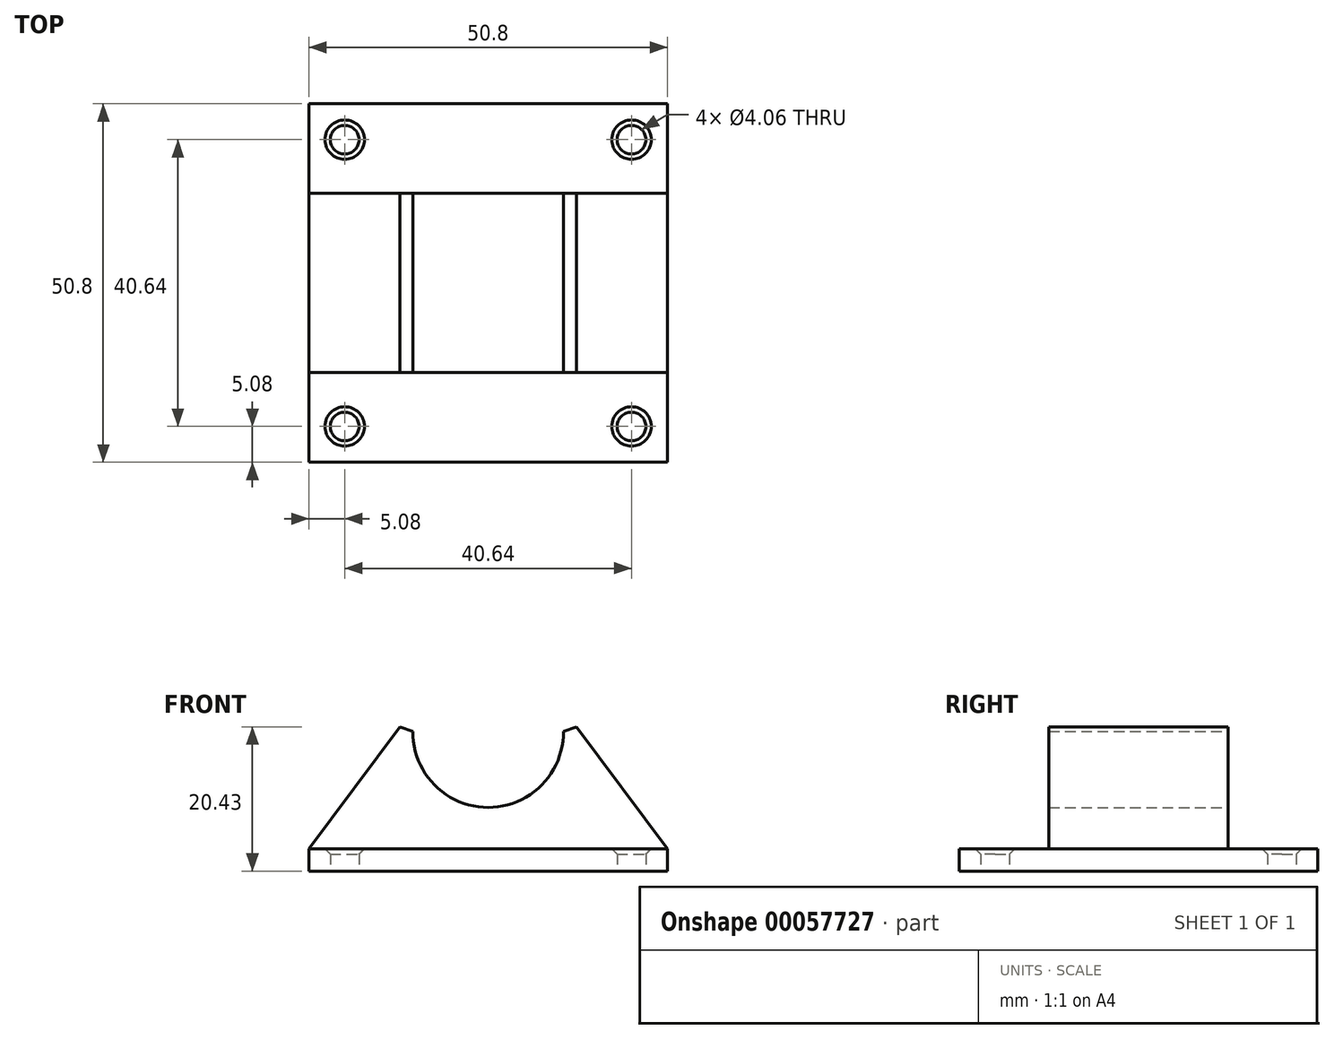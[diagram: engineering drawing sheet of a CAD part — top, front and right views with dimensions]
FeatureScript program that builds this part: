
annotation { "Feature Type Name" : "Feature", "Feature Type Description" : "" }
export const myFeature = defineFeature(function(context is Context, id is Id, definition is map)
    precondition{}
    {
        {
            var Q0;
            Q0=qCreatedBy(makeId("Top.planeOp"),FACE);
            var sketch = newSketch(context, id + "F0", { "sketchPlane" : qUnion([Q0])});
            skLineSegment(sketch, "E0.rect.bottom", {"start": v(-25.4, 25.4) * mm, "end": v(25.4, 25.4) * mm});
            skLineSegment(sketch, "E0.rect.top", {"start": v(-25.4, -25.4) * mm, "end": v(25.4, -25.4) * mm});
            skLineSegment(sketch, "E0.rect.left", {"start": v(-25.4, 25.4) * mm, "end": v(-25.4, -25.4) * mm});
            skLineSegment(sketch, "E0.rect.right", {"start": v(25.4, 25.4) * mm, "end": v(25.4, -25.4) * mm});
            skPoint(sketch, "E0.rect.middle", {"position": v(0, 0) * mm});
            skSolve(sketch);
        }
        {
            var Q0;
            Q0=makeQuery(id+"F0.imprint","IMPRINT",FACE,{"disambiguationData":[TD([[makeQuery(id+"F0.imprint","IMPRINT",EDGE,{"derivedFrom":sQuery(id+"F0.wireOp",EDGE,"E0.rect.bottom")}),-1.0]])]});
            extrude(context, id + "F1", {"entities" : qUnion([Q0]), "depth" : 3.17 * mm});
        }
        {
            var Q0;
            Q0=qCreatedBy(makeId("Front.planeOp"),FACE);
            var sketch = newSketch(context, id + "F2", { "sketchPlane" : qUnion([Q0])});
            skArc(sketch, "E1", {"start": v(-9.64, 24.26) * mm, "mid": v(0, 9.02) * mm, "end": v(9.64, 24.26) * mm});
            skLineSegment(sketch, "E2", {"start": v(9.64, 24.26) * mm, "end": v(-9.64, 24.26) * mm, "construction": true});
            skLineSegment(sketch, "E3.0", {"start": v(-25.4, 3.18) * mm, "end": v(25.4, 3.18) * mm});
            skLineSegment(sketch, "E4", {"start": v(-9.64, 24.26) * mm, "end": v(-25.4, 3.17) * mm});
            skLineSegment(sketch, "E5", {"start": v(9.64, 24.26) * mm, "end": v(25.4, 3.18) * mm});
            skSolve(sketch);
        }
        {
            var Q0;
            Q0=makeQuery(id+"F2.imprint","IMPRINT",FACE,{"disambiguationData":[TD([[makeQuery(id+"F2.imprint","IMPRINT",EDGE,{"derivedFrom":sQuery(id+"F2.wireOp",EDGE,"E1")}),-1.0]])]});
            extrude(context, id + "F3", {"entities" : qUnion([Q0]), "operationType" : NewBodyOperationType.ADD, "endBound" : BoundingType.SYMMETRIC, "depth" : 25.4 * mm});
        }
        {
            var Q0;
            Q0=makeQuery(id+"F3.opExtrude","SWEPT_EDGE",EDGE,{"disambiguationData":[OSD([sQuery(id+"F2.wireOp",EDGE,"E1"),sQuery(id+"F2.wireOp",EDGE,"E4")])]});
            var Q1;
            Q1=makeQuery(id+"F3.opExtrude","SWEPT_EDGE",EDGE,{"disambiguationData":[OSD([sQuery(id+"F2.wireOp",EDGE,"E1"),sQuery(id+"F2.wireOp",EDGE,"E5")])]});
            chamfer(context, id + "F4", {"entities" : qUnion([Q0, Q1]), "width" : 1.02 * mm, "tangentPropagation" : true});
        }
        {
            var Q0;
            Q0=makeQuery(id+"F1.opExtrude","CAP_FACE",FACE,{"disambiguationData":[OSD([sQuery(id+"F0.wireOp",EDGE,"E0.rect.bottom"),sQuery(id+"F0.wireOp",EDGE,"E0.rect.top"),sQuery(id+"F0.wireOp",EDGE,"E0.rect.left"),sQuery(id+"F0.wireOp",EDGE,"E0.rect.right")])],"isStart":true});
            var sketch = newSketch(context, id + "F5", { "sketchPlane" : qUnion([Q0])});
            skLineSegment(sketch, "E6.0", {"start": v(-20.32, 20.32) * mm, "end": v(20.32, 20.32) * mm, "construction": true});
            skLineSegment(sketch, "E6.1", {"start": v(-20.32, -20.32) * mm, "end": v(-20.32, 20.32) * mm, "construction": true});
            skLineSegment(sketch, "E6.2", {"start": v(-20.32, -20.32) * mm, "end": v(20.32, -20.32) * mm, "construction": true});
            skLineSegment(sketch, "E6.3", {"start": v(20.32, -20.32) * mm, "end": v(20.32, 20.32) * mm, "construction": true});
            skCircle(sketch, "E7", {"center": v(-20.32, 20.32) * mm, "radius": 2.03 * mm});
            skCircle(sketch, "E8", {"center": v(20.32, 20.32) * mm, "radius": 2.03 * mm});
            skCircle(sketch, "E9", {"center": v(20.32, -20.32) * mm, "radius": 2.03 * mm});
            skCircle(sketch, "E10", {"center": v(-20.32, -20.32) * mm, "radius": 2.03 * mm});
            skSolve(sketch);
        }
        {
            var Q0;
            Q0=makeQuery(id+"F5.imprint","IMPRINT",FACE,{"disambiguationData":[TD([[makeQuery(id+"F5.imprint","IMPRINT",EDGE,{"derivedFrom":sQuery(id+"F5.wireOp",EDGE,"E7")}),1.0]])]});
            var Q1;
            Q1=makeQuery(id+"F5.imprint","IMPRINT",FACE,{"disambiguationData":[TD([[makeQuery(id+"F5.imprint","IMPRINT",EDGE,{"derivedFrom":sQuery(id+"F5.wireOp",EDGE,"E10")}),1.0]])]});
            var Q2;
            Q2=makeQuery(id+"F5.imprint","IMPRINT",FACE,{"disambiguationData":[TD([[makeQuery(id+"F5.imprint","IMPRINT",EDGE,{"derivedFrom":sQuery(id+"F5.wireOp",EDGE,"E8")}),1.0]])]});
            var Q3;
            Q3=makeQuery(id+"F5.imprint","IMPRINT",FACE,{"disambiguationData":[TD([[makeQuery(id+"F5.imprint","IMPRINT",EDGE,{"derivedFrom":sQuery(id+"F5.wireOp",EDGE,"E9")}),1.0]])]});
            var Q4;
            Q4=sQuery(id+"F5.wireOp",EDGE,"E7");
            var Q5;
            Q5=sQuery(id+"F5.wireOp",EDGE,"E10");
            var Q6;
            Q6=sQuery(id+"F5.wireOp",EDGE,"E9");
            var Q7;
            Q7=sQuery(id+"F5.wireOp",EDGE,"E8");
            extrude(context, id + "F6", {"entities" : qUnion([Q0, Q1, Q2, Q3]), "operationType" : NewBodyOperationType.REMOVE, "surfaceEntities" : qUnion([Q4, Q5, Q6, Q7]), "oppositeDirection" : true, "depth" : 25.4 * mm});
        }
        {
            var Q0;
            {var subQ2=sQuery(id+"F0.wireOp",EDGE,"E0.rect.right");var subQ3=sQuery(id+"F0.wireOp",EDGE,"E0.rect.left");var subQ4=sQuery(id+"F0.wireOp",EDGE,"E0.rect.top");Q0=makeQuery(id+"F6.boolean.opBoolean","INTERSECT",EDGE,{"derivedFrom":[makeQuery(id+"F3.boolean.opBoolean","SPLIT",FACE,{"disambiguationData":[TD([makeQuery(id+"F1.opExtrude","SWEPT_FACE",FACE,{"disambiguationData":[OSD([subQ4])]})])],"derivedFrom":makeQuery(id+"F1.opExtrude","CAP_FACE",FACE,{"disambiguationData":[OSD([sQuery(id+"F0.wireOp",EDGE,"E0.rect.bottom"),subQ4,subQ3,subQ2])],"isStart":false})}),makeQuery(id+"F6.opExtrude","SWEPT_FACE",FACE,{"disambiguationData":[OSD([sQuery(id+"F5.wireOp",EDGE,"E7")])]})]});}
            var Q1;
            {var subQ0=sQuery(id+"F0.wireOp",EDGE,"E0.rect.right");var subQ1=sQuery(id+"F0.wireOp",EDGE,"E0.rect.left");var subQ4=sQuery(id+"F0.wireOp",EDGE,"E0.rect.bottom");Q1=makeQuery(id+"F6.boolean.opBoolean","INTERSECT",EDGE,{"derivedFrom":[makeQuery(id+"F3.boolean.opBoolean","SPLIT",FACE,{"disambiguationData":[TD([makeQuery(id+"F1.opExtrude","SWEPT_FACE",FACE,{"disambiguationData":[OSD([subQ4])]})])],"derivedFrom":makeQuery(id+"F1.opExtrude","CAP_FACE",FACE,{"disambiguationData":[OSD([subQ4,sQuery(id+"F0.wireOp",EDGE,"E0.rect.top"),subQ1,subQ0])],"isStart":false})}),makeQuery(id+"F6.opExtrude","SWEPT_FACE",FACE,{"disambiguationData":[OSD([sQuery(id+"F5.wireOp",EDGE,"E10")])]})]});}
            var Q2;
            {var subQ0=sQuery(id+"F0.wireOp",EDGE,"E0.rect.right");var subQ1=sQuery(id+"F0.wireOp",EDGE,"E0.rect.left");var subQ4=sQuery(id+"F0.wireOp",EDGE,"E0.rect.bottom");Q2=makeQuery(id+"F6.boolean.opBoolean","INTERSECT",EDGE,{"derivedFrom":[makeQuery(id+"F3.boolean.opBoolean","SPLIT",FACE,{"disambiguationData":[TD([makeQuery(id+"F1.opExtrude","SWEPT_FACE",FACE,{"disambiguationData":[OSD([subQ4])]})])],"derivedFrom":makeQuery(id+"F1.opExtrude","CAP_FACE",FACE,{"disambiguationData":[OSD([subQ4,sQuery(id+"F0.wireOp",EDGE,"E0.rect.top"),subQ1,subQ0])],"isStart":false})}),makeQuery(id+"F6.opExtrude","SWEPT_FACE",FACE,{"disambiguationData":[OSD([sQuery(id+"F5.wireOp",EDGE,"E9")])]})]});}
            var Q3;
            {var subQ2=sQuery(id+"F0.wireOp",EDGE,"E0.rect.right");var subQ3=sQuery(id+"F0.wireOp",EDGE,"E0.rect.left");var subQ4=sQuery(id+"F0.wireOp",EDGE,"E0.rect.top");Q3=makeQuery(id+"F6.boolean.opBoolean","INTERSECT",EDGE,{"derivedFrom":[makeQuery(id+"F3.boolean.opBoolean","SPLIT",FACE,{"disambiguationData":[TD([makeQuery(id+"F1.opExtrude","SWEPT_FACE",FACE,{"disambiguationData":[OSD([subQ4])]})])],"derivedFrom":makeQuery(id+"F1.opExtrude","CAP_FACE",FACE,{"disambiguationData":[OSD([sQuery(id+"F0.wireOp",EDGE,"E0.rect.bottom"),subQ4,subQ3,subQ2])],"isStart":false})}),makeQuery(id+"F6.opExtrude","SWEPT_FACE",FACE,{"disambiguationData":[OSD([sQuery(id+"F5.wireOp",EDGE,"E8")])]})]});}
            chamfer(context, id + "F7", {"entities" : qUnion([Q0, Q1, Q2, Q3]), "width" : 0.76 * mm, "tangentPropagation" : true});
        }
    });
